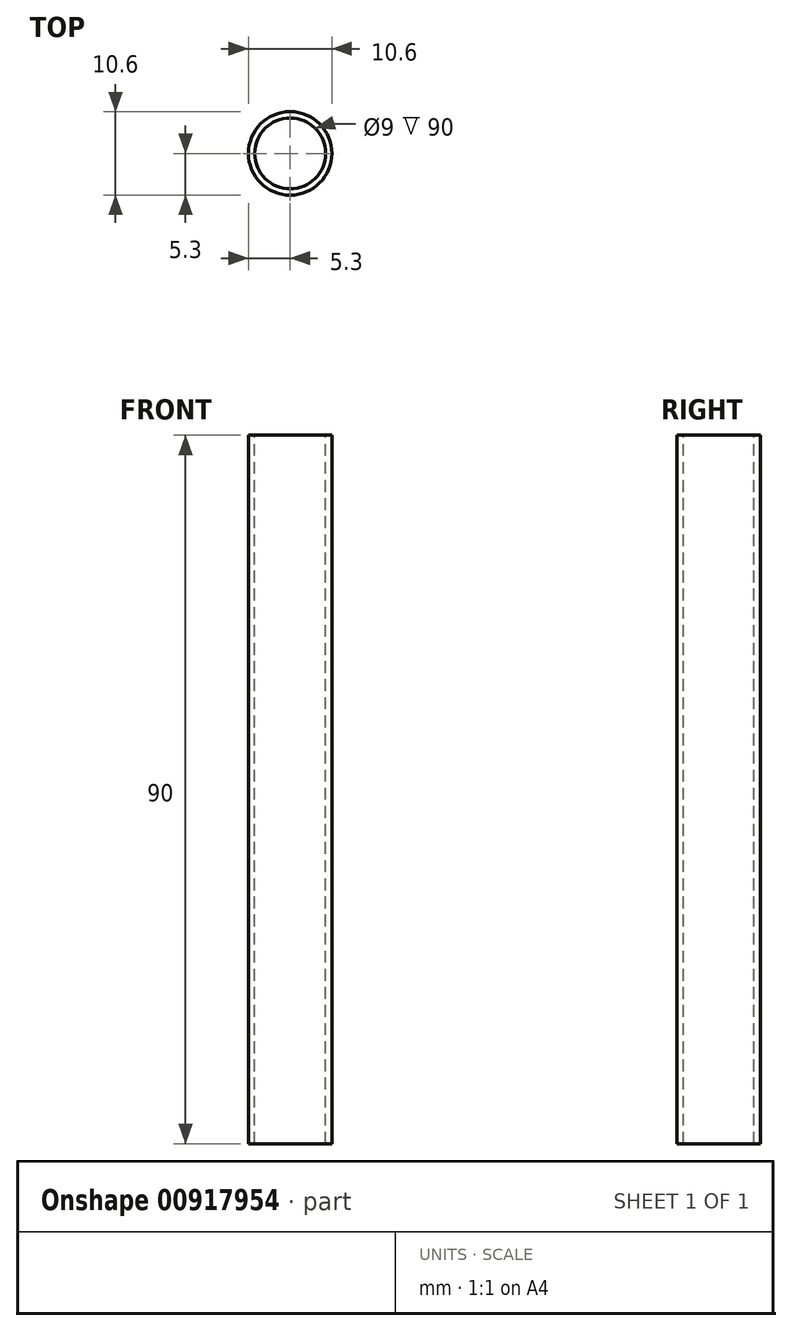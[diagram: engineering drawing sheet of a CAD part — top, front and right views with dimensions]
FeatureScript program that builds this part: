
annotation { "Feature Type Name" : "Feature", "Feature Type Description" : "" }
export const myFeature = defineFeature(function(context is Context, id is Id, definition is map)
    precondition{}
    {
        {
            var Q0;
            Q0=qCreatedBy(makeId("Top.planeOp"),FACE);
            var sketch = newSketch(context, id + "F0", { "sketchPlane" : qUnion([Q0])});
            skCircle(sketch, "E0", {"center": v(0, 0) * mm, "radius": 5.3 * mm});
            skSolve(sketch);
        }
        {
            var Q0;
            Q0=qCreatedBy(makeId("Top.planeOp"),FACE);
            var sketch = newSketch(context, id + "F1", { "sketchPlane" : qUnion([Q0])});
            skCircle(sketch, "E1", {"center": v(0, 0) * mm, "radius": 4.5 * mm});
            skSolve(sketch);
        }
        {
            var Q0;
            Q0=makeQuery(id+"F0.imprint","IMPRINT",FACE,{"disambiguationData":[TD([[makeQuery(id+"F0.imprint","IMPRINT",EDGE,{"derivedFrom":sQuery(id+"F0.wireOp",EDGE,"E0")}),1.0]])]});
            extrude(context, id + "F2", {"entities" : qUnion([Q0]), "oppositeDirection" : true, "depth" : 90 * mm, "offsetDistance" : 25.4 * mm});
        }
        {
            var Q0;
            Q0=sQuery(id+"F1.wireOp",VERTEX,"E1.center");
            var Q1;
            Q1=makeQuery(id+"F2.opExtrude","SWEPT_BODY",BODY,{"disambiguationData":[OSD([sQuery(id+"F0.wireOp",EDGE,"E0")])]});
            hole(context, id + "F3", {"style" : HoleStyle.SIMPLE, "endStyle" : HoleEndStyle.THROUGH, "holeDiameter" : 9 * mm, "majorDiameter" : 6.35 * mm, "isTappedThrough" : true, "tappedDepth" : 12.7 * mm, "tapClearance" : 3, "locations" : qUnion([Q0]), "scope" : qUnion([Q1])});
        }
    });
